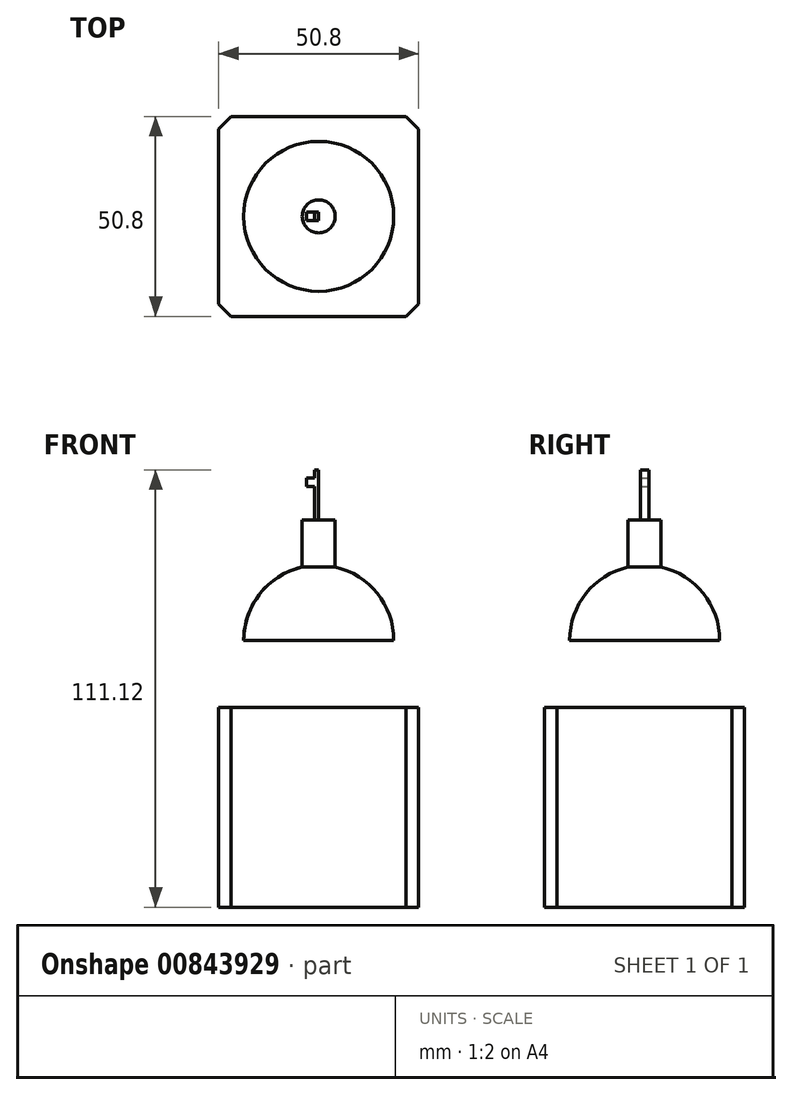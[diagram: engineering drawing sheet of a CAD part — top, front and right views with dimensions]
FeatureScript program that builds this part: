
annotation { "Feature Type Name" : "Feature", "Feature Type Description" : "" }
export const myFeature = defineFeature(function(context is Context, id is Id, definition is map)
    precondition{}
    {
        {
            var Q0;
            Q0=qCreatedBy(makeId("Top.planeOp"),FACE);
            var sketch = newSketch(context, id + "F0", { "sketchPlane" : qUnion([Q0])});
            skLineSegment(sketch, "E0.bottom", {"start": v(25.4, 25.4) * mm, "end": v(-25.4, 25.4) * mm});
            skLineSegment(sketch, "E0.top", {"start": v(25.4, -25.4) * mm, "end": v(-25.4, -25.4) * mm});
            skLineSegment(sketch, "E0.left", {"start": v(25.4, 25.4) * mm, "end": v(25.4, -25.4) * mm});
            skLineSegment(sketch, "E0.right", {"start": v(-25.4, 25.4) * mm, "end": v(-25.4, -25.4) * mm});
            skPoint(sketch, "E0.middle", {"position": v(0, 0) * mm});
            skSolve(sketch);
        }
        {
            var Q0;
            Q0 = qSketchRegion(id + "F0", true);
            extrude(context, id + "F1", {"entities" : qUnion([Q0]), "depth" : 50.8 * mm, "offsetDistance" : 25.4 * mm});
        }
        {
            var Q0;
            {var subQ0=sQuery(id+"F0.wireOp",EDGE,"E0.right");var subQ1=sQuery(id+"F0.wireOp",EDGE,"E0.top");Q0=makeQuery(id+"F9hONZeCB7BHPof_1.boolean.opBoolean","MERGE",EDGE,{"derivedFrom":[makeQuery(id+"FGvphdm9WWL0dMd_1.boolean.opBoolean","MERGE",EDGE,{"derivedFrom":[makeQuery(id+"FaQovxJeUx2Pmob_1.boolean.opBoolean","MERGE",EDGE,{"derivedFrom":[makeQuery(id+"F1.opExtrude","SWEPT_EDGE",EDGE,{"disambiguationData":[OSD([subQ1,subQ0])]}),makeQuery(id+"FaQovxJeUx2Pmob_1.opExtrude","SWEPT_EDGE",EDGE,{"disambiguationData":[OSD([subQ1,subQ0])]})]}),makeQuery(id+"FGvphdm9WWL0dMd_1.opExtrude","SWEPT_EDGE",EDGE,{"disambiguationData":[OSD([subQ1,subQ0])]})]}),makeQuery(id+"F9hONZeCB7BHPof_1.opExtrude","SWEPT_EDGE",EDGE,{"disambiguationData":[OSD([subQ1,subQ0])]})]});}
            var Q1;
            {var subQ0=sQuery(id+"F0.wireOp",EDGE,"E0.left");var subQ1=sQuery(id+"F0.wireOp",EDGE,"E0.top");Q1=makeQuery(id+"F9hONZeCB7BHPof_1.boolean.opBoolean","MERGE",EDGE,{"derivedFrom":[makeQuery(id+"FGvphdm9WWL0dMd_1.boolean.opBoolean","MERGE",EDGE,{"derivedFrom":[makeQuery(id+"FaQovxJeUx2Pmob_1.boolean.opBoolean","MERGE",EDGE,{"derivedFrom":[makeQuery(id+"F1.opExtrude","SWEPT_EDGE",EDGE,{"disambiguationData":[OSD([subQ1,subQ0])]}),makeQuery(id+"FaQovxJeUx2Pmob_1.opExtrude","SWEPT_EDGE",EDGE,{"disambiguationData":[OSD([subQ1,subQ0])]})]}),makeQuery(id+"FGvphdm9WWL0dMd_1.opExtrude","SWEPT_EDGE",EDGE,{"disambiguationData":[OSD([subQ1,subQ0])]})]}),makeQuery(id+"F9hONZeCB7BHPof_1.opExtrude","SWEPT_EDGE",EDGE,{"disambiguationData":[OSD([subQ1,subQ0])]})]});}
            var Q2;
            {var subQ0=sQuery(id+"F0.wireOp",EDGE,"E0.left");var subQ1=sQuery(id+"F0.wireOp",EDGE,"E0.bottom");Q2=makeQuery(id+"F9hONZeCB7BHPof_1.boolean.opBoolean","MERGE",EDGE,{"derivedFrom":[makeQuery(id+"FGvphdm9WWL0dMd_1.boolean.opBoolean","MERGE",EDGE,{"derivedFrom":[makeQuery(id+"FaQovxJeUx2Pmob_1.boolean.opBoolean","MERGE",EDGE,{"derivedFrom":[makeQuery(id+"F1.opExtrude","SWEPT_EDGE",EDGE,{"disambiguationData":[OSD([subQ1,subQ0])]}),makeQuery(id+"FaQovxJeUx2Pmob_1.opExtrude","SWEPT_EDGE",EDGE,{"disambiguationData":[OSD([subQ1,subQ0])]})]}),makeQuery(id+"FGvphdm9WWL0dMd_1.opExtrude","SWEPT_EDGE",EDGE,{"disambiguationData":[OSD([subQ1,subQ0])]})]}),makeQuery(id+"F9hONZeCB7BHPof_1.opExtrude","SWEPT_EDGE",EDGE,{"disambiguationData":[OSD([subQ1,subQ0])]})]});}
            var Q3;
            {var subQ0=sQuery(id+"F0.wireOp",EDGE,"E0.right");var subQ1=sQuery(id+"F0.wireOp",EDGE,"E0.bottom");Q3=makeQuery(id+"F9hONZeCB7BHPof_1.boolean.opBoolean","MERGE",EDGE,{"derivedFrom":[makeQuery(id+"FGvphdm9WWL0dMd_1.boolean.opBoolean","MERGE",EDGE,{"derivedFrom":[makeQuery(id+"FaQovxJeUx2Pmob_1.boolean.opBoolean","MERGE",EDGE,{"derivedFrom":[makeQuery(id+"F1.opExtrude","SWEPT_EDGE",EDGE,{"disambiguationData":[OSD([subQ1,subQ0])]}),makeQuery(id+"FaQovxJeUx2Pmob_1.opExtrude","SWEPT_EDGE",EDGE,{"disambiguationData":[OSD([subQ1,subQ0])]})]}),makeQuery(id+"FGvphdm9WWL0dMd_1.opExtrude","SWEPT_EDGE",EDGE,{"disambiguationData":[OSD([subQ1,subQ0])]})]}),makeQuery(id+"F9hONZeCB7BHPof_1.opExtrude","SWEPT_EDGE",EDGE,{"disambiguationData":[OSD([subQ1,subQ0])]})]});}
            chamfer(context, id + "F2", {"entities" : qUnion([Q0, Q1, Q2, Q3]), "width" : 3.17 * mm, "tangentPropagation" : true});
        }
        {
            var Q0;
            Q0=qCreatedBy(makeId("Front.planeOp"),FACE);
            var sketch = newSketch(context, id + "F3", { "sketchPlane" : qUnion([Q0])});
            skPoint(sketch, "E1.0", {"position": v(0, 50.8) * mm});
            skLineSegment(sketch, "E2.0.0", {"start": v(22.22, 50.8) * mm, "end": v(-22.23, 50.8) * mm});
            skLineSegment(sketch, "E2.0.1", {"start": v(-22.23, 50.8) * mm, "end": v(-25.4, 50.8) * mm});
            skLineSegment(sketch, "E2.0.3", {"start": v(-25.4, 50.8) * mm, "end": v(-22.22, 50.8) * mm});
            skLineSegment(sketch, "E2.0.4", {"start": v(-22.23, 50.8) * mm, "end": v(22.23, 50.8) * mm});
            skLineSegment(sketch, "E2.0.5", {"start": v(22.23, 50.8) * mm, "end": v(25.4, 50.8) * mm});
            skLineSegment(sketch, "E2.0.7", {"start": v(25.4, 50.8) * mm, "end": v(22.22, 50.8) * mm});
            skLineSegment(sketch, "E3.bottom", {"start": v(0, 50.8) * mm, "end": v(-19.05, 50.8) * mm});
            skLineSegment(sketch, "E3.top", {"start": v(0, 67.82) * mm, "end": v(-19.05, 67.82) * mm});
            skLineSegment(sketch, "E3.left", {"start": v(0, 50.8) * mm, "end": v(0, 67.82) * mm});
            skLineSegment(sketch, "E3.right", {"start": v(-19.05, 50.8) * mm, "end": v(-19.05, 67.82) * mm});
            skArc(sketch, "E4", {"start": v(-19.05, 67.82) * mm, "mid": v(-14.88, 79.71) * mm, "end": v(-4.2, 86.4) * mm});
            skLineSegment(sketch, "E5", {"start": v(0, 86.87) * mm, "end": v(0, 67.82) * mm});
            skLineSegment(sketch, "E6.bottom", {"start": v(-4.2, 86.4) * mm, "end": v(0, 86.4) * mm});
            skLineSegment(sketch, "E6.top", {"start": v(-4.2, 98.43) * mm, "end": v(0, 98.43) * mm});
            skLineSegment(sketch, "E6.left", {"start": v(-4.2, 86.4) * mm, "end": v(-4.2, 98.43) * mm});
            skLineSegment(sketch, "E6.right", {"start": v(0, 86.4) * mm, "end": v(0, 98.43) * mm});
            skSolve(sketch);
        }
        {
            var Q0;
            Q0=makeQuery(id+"F3.imprint","IMPRINT",FACE,{"disambiguationData":[TD([[makeQuery(id+"F3.imprint","IMPRINT",EDGE,{"derivedFrom":sQuery(id+"F3.wireOp",EDGE,"E3.bottom")}),-1.0]])]});
            var Q1;
            Q1=makeQuery(id+"F3.imprint","IMPRINT",FACE,{"disambiguationData":[TD([[makeQuery(id+"F3.imprint","IMPRINT",EDGE,{"derivedFrom":sQuery(id+"F3.wireOp",EDGE,"E3.top")}),-1.0]])]});
            var Q2;
            {var subQ0=sQuery(id+"F3.wireOp",EDGE,"E6.bottom");Q2=makeQuery(id+"F3.imprint","IMPRINT",FACE,{"disambiguationData":[TD([[makeQuery(id+"F3.imprint","IMPRINT",EDGE,{"derivedFrom":subQ0}),1.0]])]});}
            var Q3;
            Q3=sQuery(id+"F3.wireOp",EDGE,"E3.left");
            revolve(context, id + "F4", {"operationType" : NewBodyOperationType.ADD, "surfaceOperationType" : NewSurfaceOperationType.NEW, "entities" : qUnion([Q0, Q1, Q2]), "axis" : qUnion([Q3]), "revolveType" : RevolveType.FULL});
        }
        {
            var Q0;
            Q0=qCreatedBy(makeId("Front.planeOp"),FACE);
            var sketch = newSketch(context, id + "F5", { "sketchPlane" : qUnion([Q0])});
            skLineSegment(sketch, "E7.0", {"start": v(4.2, 98.43) * mm, "end": v(-4.2, 98.43) * mm});
            skLineSegment(sketch, "E8.bottom", {"start": v(0, 98.43) * mm, "end": v(-1.05, 98.43) * mm});
            skLineSegment(sketch, "E8.top", {"start": v(0, 111.13) * mm, "end": v(-1.05, 111.13) * mm});
            skLineSegment(sketch, "E8.left", {"start": v(0, 98.43) * mm, "end": v(0, 111.13) * mm});
            skLineSegment(sketch, "E8.right", {"start": v(-1.05, 98.43) * mm, "end": v(-1.05, 111.13) * mm});
            skLineSegment(sketch, "E9.bottom", {"start": v(-1.05, 109.02) * mm, "end": v(-3.16, 109.02) * mm});
            skLineSegment(sketch, "E9.top", {"start": v(-1.05, 106.9) * mm, "end": v(-3.16, 106.9) * mm});
            skLineSegment(sketch, "E9.left", {"start": v(-1.05, 109.02) * mm, "end": v(-1.05, 106.9) * mm});
            skLineSegment(sketch, "E9.right", {"start": v(-3.16, 109.02) * mm, "end": v(-3.16, 106.9) * mm});
            skSolve(sketch);
        }
        {
            var Q0;
            {var subQ0=sQuery(id+"F5.wireOp",EDGE,"E9.bottom");Q0=makeQuery(id+"F5.imprint","IMPRINT",FACE,{"disambiguationData":[TD([[makeQuery(id+"F5.imprint","IMPRINT",EDGE,{"derivedFrom":subQ0}),1.0]])]});}
            var Q1;
            {var subQ5=sQuery(id+"F5.wireOp",EDGE,"E8.top");Q1=makeQuery(id+"F5.imprint","IMPRINT",FACE,{"disambiguationData":[TD([[makeQuery(id+"F5.imprint","IMPRINT",EDGE,{"derivedFrom":subQ5}),1.0]])]});}
            extrude(context, id + "F6", {"entities" : qUnion([Q0, Q1]), "operationType" : NewBodyOperationType.ADD, "depth" : 2.1 * mm, "offsetDistance" : 25.4 * mm, "symmetric" : true});
        }
        {
            var Q0;
            Q0=makeQuery(id+"F1.opExtrude","SWEPT_BODY",BODY,{"disambiguationData":[OSD([sQuery(id+"F0.wireOp",EDGE,"E0.bottom"),sQuery(id+"F0.wireOp",EDGE,"E0.top"),sQuery(id+"F0.wireOp",EDGE,"E0.left"),sQuery(id+"F0.wireOp",EDGE,"E0.right")])]});
            var Q1;
            Q1=makeQuery(id+"F6.opExtrude","SWEPT_FACE",FACE,{"disambiguationData":[OSD([sQuery(id+"F5.wireOp",EDGE,"E8.left")])]});
            mirror(context, id + "F7", {"operationType" : NewBodyOperationType.ADD, "entities" : qUnion([Q0]), "mirrorPlane" : qUnion([Q1])});
        }
    });
